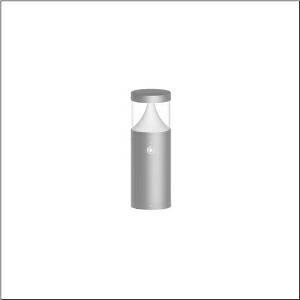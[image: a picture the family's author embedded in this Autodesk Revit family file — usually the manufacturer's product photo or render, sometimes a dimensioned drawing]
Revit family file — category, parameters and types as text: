
# Revit family: cl_31_poller_40_sensor_5cl424803
name_source: partatom
category: Lighting Fixtures
units: mm (PartAtom-declared; Revit-internal decimal feet)

## family parameters
Cut with Voids When Loaded = No
Host = Face
Light Source = No
Part Type = Normal
Room Calculation Point = No
Round Connector Dimension = Use Diameter
Shared = No

## types (1)
- --- (1 x LED, 800 lm, 7.2 W, 3000K)
    Apparent Load = 7 VA
    CIE Flux Codes = 19 66 88 92 100
    Color Rendering = 80
    Color Temperature = 3000K
    Default Elevation = 1800 mm
    Description = CL 31 Bollard 40 Sensor, bollard luminaire, primary light control with lens, of PC, primary optical cover: cover panel, of PC, transparent, secondary light control with reflector, of PC, primary light characteristic: asymmetric, LED, rated luminous flux: 800lm, luminous efficacy: 110lm/W, light colour: 830, colour temperature: 3000K, control gear: DALI, with terminal, 5-pole, max. 2.5mm², mains connection: 220..240V, AC, 50/60Hz, rated input power: 7.2W, luminaire housing, of aluminium, powder-coated, SITECO metallic grey, diameter: 170mm, height: 400mm, PIR sensor, protection rating (complete): IP65, insulation class (complete): insulation class I (protective earthing), certification: CE, ENEC, impact resistance: IK08, permissible operating ambient temperature for outdoor applications: -20..+50°C, packaging unit: 1 piece
    Height = 200 mm  [stored 0.656168 ft]
    Lamp = 1 x LED
    Lamp Light Flux = 800 lm
    Lamp Power = 7.2 W
    Lamp count = 1
    Length = 170 mm  [stored 0.557743 ft]
    Luminous efficacy = 111 lm/W
    Manufacturer = Siteco
    ModVariant = No
    Model = 5CL424803
    Mounting Place = Floor
    Mounting Type = Freestanding
    Number of Poles = 1
    OnlyDefault = Yes
    Power Factor = 1
    Product Name = CL 31 Poller 40 Sensor
    Product group = bollard luminaire
    ProductGroupID = 1304
    Protection Class = Protection class I
    Protection Degree = IP 65
    RLX_Detail_Level = 1
    RLX_Emergency_Light_Flux = 0 lm
    RLX_Emergency_Type = 0
    RLX_Emergency_Type_DB = No
    RlxData = <blob elided: 62761 chars, md5=c1995b3d>
    Socket = socket
    Standby Power = 0 W
    System Light Flux = 800 lm
    System Power = 7 W
    Type Comments = factory setting: luminous flux: 100 % | dim-lin: 254 | 182 mA
    Type Image = l_1006905.jpg
    URL = http://relux.com
    VarID = @adj_192667
    Voltage = 0 V
    Weight = 0.00 kg
    Width = 0 mm  [stored 0 ft]

note: [stored X ft] marks values corroborated as IEEE doubles in the binary element streams (Revit-internal decimal feet)

## geometry (parser evidence)
native form markers: Blend x4, Sweep x11
no freeform markers — native parametric forms only
